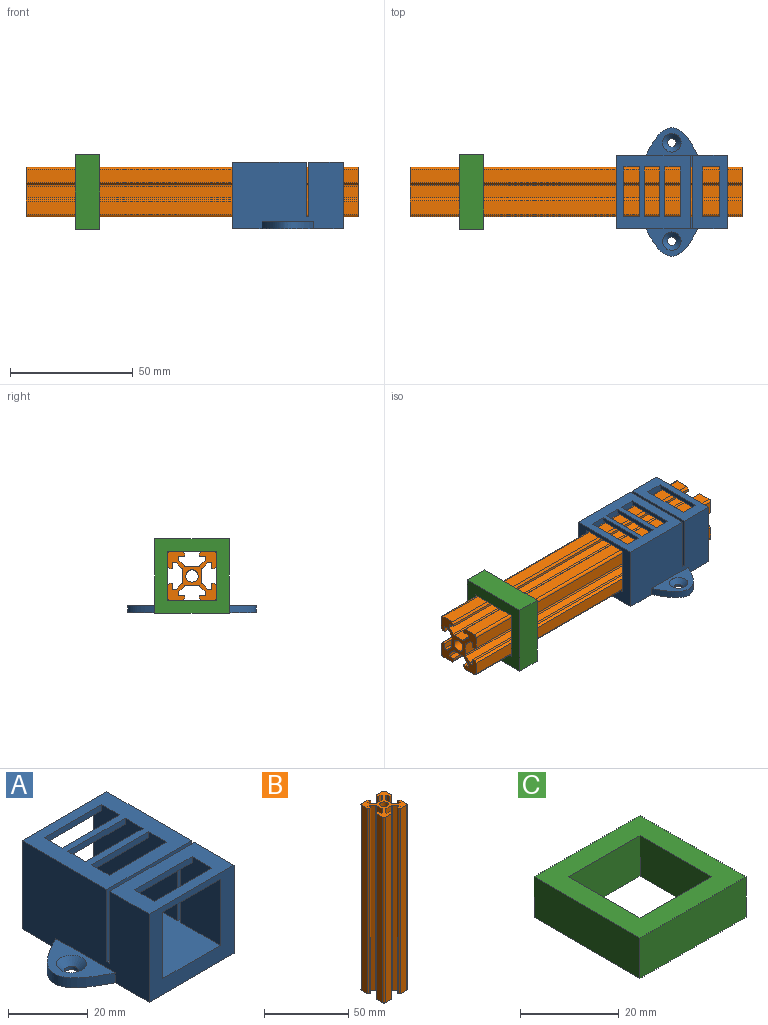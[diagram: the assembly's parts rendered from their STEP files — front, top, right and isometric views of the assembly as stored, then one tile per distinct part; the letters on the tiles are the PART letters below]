
ASSEMBLY  parts=3 mates=2
PART A: 36 faces, bbox 60.4x45x27 mm
  f0: plane 45x27mm, normal (-1,0,0), area 1129.9mm2, adj f2,f3,f11,f12,f13,f14,f16,f22
  f1: plane 45x27mm, normal (1,0,0), area 1129.9mm2, adj f2,f3,f11,f12,f13,f17,f19,f22
  f2: plane 30x30mm, normal (0,0,1), area 514.3mm2, adj f0,f1,f9,f10,f11,f24,f26,f27
  f3: plane 30x14mm, normal (0,0,1), area 277.9mm2, adj f0,f1,f12,f21,f23,f25,f32,f33
  f4: plane 20.3x4mm, normal (0,0,-1), area 81.2mm2, adj f9,f10,f24,f27
  f5: plane 20.3x4mm, normal (0,0,-1), area 81.2mm2, adj f21,f23,f25,f32
  f6: plane 20.3x3mm, normal (0,0,-1), area 60.9mm2, adj f9,f10,f11,f30
  f7: plane 20.3x2mm, normal (0,0,-1), area 40.6mm2, adj f9,f10,f29,f31
  f8: plane 20.3x2mm, normal (0,0,-1), area 40.6mm2, adj f9,f10,f26,f28
  f9: plane 30x22.15mm, normal (1,0,0), area 644.1mm2, adj f2,f4,f6,f7,f8,f11,f22,f24
  f10: plane 30x22.15mm, normal (-1,0,0), area 644.1mm2, adj f2,f4,f6,f7,f8,f11,f22,f24
  f11: plane 30x27mm, normal (0,1,0), area 397.9mm2, adj f0,f1,f2,f6,f9,f10,f13,f22
  f12: plane 30x27mm, normal (0,-1,0), area 397.9mm2, adj f0,f1,f3,f13,f20,f21,f22,f23
  f13: plane 60.43x45mm, normal (0,0,-1), area 1640.4mm2, adj f0,f1,f11,f12,f14,f15,f17,f18
  f14: extruded ~20.98x11.07mm, area 95.7mm2, adj f0,f13,f16
  f15: cylinder r=1.75mm len=3.5mm, axis (0,0,-1), area 11mm2, adj f13,f34
  f16: plane 20.98x15.22mm, normal (0,0,1), area 110.6mm2, adj f0,f14,f34
  f17: extruded ~20.98x11.07mm, area 95.7mm2, adj f1,f13,f19
  f18: cylinder r=1.75mm len=3.5mm, axis (0,0,-1), area 11mm2, adj f13,f35
  f19: plane 20.98x15.22mm, normal (0,0,1), area 110.6mm2, adj f1,f17,f35
  f20: plane 20.3x3mm, normal (0,0,-1), area 60.9mm2, adj f12,f21,f23,f33
  f21: plane 22.15x14mm, normal (1,0,0), area 297.2mm2, adj f3,f5,f12,f20,f22,f25,f32,f33
  f22: plane 45x30mm, normal (0,0,1), area 923.2mm2, adj f0,f1,f9,f10,f11,f12,f21,f23
  f23: plane 22.15x14mm, normal (-1,0,0), area 297.2mm2, adj f3,f5,f12,f20,f22,f25,f32,f33
  f24: plane 30x22.15mm, normal (0,-1,0), area 252.4mm2, adj f0,f1,f2,f4,f9,f10,f22
  f25: plane 30x22.15mm, normal (0,1,0), area 252.4mm2, adj f0,f1,f3,f5,f21,f22,f23
  f26: plane 20.3x1.85mm, normal (0,-1,0), area 37.6mm2, adj f2,f8,f9,f10
  f27: plane 20.3x1.85mm, normal (0,1,0), area 37.6mm2, adj f2,f4,f9,f10
  f28: plane 20.3x1.85mm, normal (0,1,0), area 37.6mm2, adj f2,f8,f9,f10
  f29: plane 20.3x1.85mm, normal (0,-1,0), area 37.6mm2, adj f2,f7,f9,f10
  f30: plane 20.3x1.85mm, normal (0,-1,0), area 37.6mm2, adj f2,f6,f9,f10
  f31: plane 20.3x1.85mm, normal (0,1,0), area 37.6mm2, adj f2,f7,f9,f10
  f32: plane 20.3x1.85mm, normal (0,-1,0), area 37.6mm2, adj f3,f5,f21,f23
  f33: plane 20.3x1.85mm, normal (0,1,0), area 37.6mm2, adj f3,f20,f21,f23
  f34: cone r=1.75mm half-angle=45deg, axis (0,0,1), area 48.9mm2, adj f15,f16
  f35: cone r=3.75mm half-angle=45deg, axis (0,0,1), area 48.9mm2, adj f18,f19
PART B: 75 faces, bbox 20x20x135 mm
  f0: plane 135x1mm, normal (1,0,0), area 135mm2, adj f1,f71,f73,f74
  f1: plane 135x1mm, normal (0.82,0.57,0), area 164.8mm2, adj f0,f2,f73,f74
  f2: plane 135x5.3mm, normal (0,1,0), area 715.5mm2, adj f1,f3,f73,f74
  f3: cylinder r=1mm len=135mm, axis (0,0,-1), area 212.1mm2, adj f2,f4,f73,f74
  f4: plane 135x5.3mm, normal (-1,0,0), area 715.5mm2, adj f3,f5,f73,f74
  f5: plane 135x1mm, normal (-0.57,-0.82,0), area 164.8mm2, adj f4,f6,f73,f74
  f6: plane 135x1mm, normal (0,-1,0), area 135mm2, adj f5,f7,f73,f74
  f7: plane 135x2.5mm, normal (1,0,0), area 337.5mm2, adj f6,f8,f73,f74
  f8: plane 135x1.23mm, normal (0,-1,0), area 166.4mm2, adj f7,f9,f73,f74
  f9: cylinder r=0.5mm len=135mm, axis (0,0,-1), area 53mm2, adj f8,f10,f73,f74
  f10: plane 135x2.22mm, normal (-0.71,-0.71,0), area 424.1mm2, adj f9,f11,f73,f74
  f11: cylinder r=1mm len=135mm, axis (0,0,-1), area 106mm2, adj f10,f12,f73,f74
  f12: plane 135x4.85mm, normal (-1,0,0), area 654.8mm2, adj f11,f13,f73,f74
  f13: cylinder r=1mm len=135mm, axis (0,0,-1), area 106mm2, adj f12,f14,f73,f74
  f14: plane 135x2.22mm, normal (-0.71,0.71,0), area 424.1mm2, adj f13,f15,f73,f74
  f15: cylinder r=0.5mm len=135mm, axis (0,0,-1), area 53mm2, adj f14,f16,f73,f74
  f16: plane 135x1.23mm, normal (0,1,0), area 166.4mm2, adj f15,f17,f73,f74
  f17: plane 135x2.5mm, normal (1,0,0), area 337.5mm2, adj f16,f18,f73,f74
  f18: plane 135x1mm, normal (0,1,0), area 135mm2, adj f17,f19,f73,f74
  f19: plane 135x1mm, normal (-0.57,0.82,0), area 164.8mm2, adj f18,f20,f73,f74
  f20: plane 135x5.3mm, normal (-1,0,0), area 715.5mm2, adj f19,f21,f73,f74
  f21: cylinder r=1mm len=135mm, axis (0,0,-1), area 212.1mm2, adj f20,f22,f73,f74
  f22: plane 135x5.3mm, normal (0,-1,0), area 715.5mm2, adj f21,f23,f73,f74
  f23: plane 135x1mm, normal (0.82,-0.57,0), area 164.8mm2, adj f22,f24,f73,f74
  f24: plane 135x1mm, normal (1,0,0), area 135mm2, adj f23,f25,f73,f74
  f25: plane 135x2.5mm, normal (0,1,0), area 337.5mm2, adj f24,f26,f73,f74
  f26: plane 135x1.23mm, normal (1,0,0), area 166.4mm2, adj f25,f27,f73,f74
  f27: cylinder r=0.5mm len=135mm, axis (0,0,-1), area 53mm2, adj f26,f28,f73,f74
  f28: plane 135x2.22mm, normal (0.71,-0.71,0), area 424.1mm2, adj f27,f29,f73,f74
  f29: cylinder r=1mm len=135mm, axis (0,0,-1), area 106mm2, adj f28,f30,f73,f74
  f30: plane 135x4.85mm, normal (0,-1,0), area 654.8mm2, adj f29,f31,f73,f74
  f31: cylinder r=1mm len=135mm, axis (0,0,-1), area 106mm2, adj f30,f32,f73,f74
  f32: plane 135x2.22mm, normal (-0.71,-0.71,0), area 424.1mm2, adj f31,f33,f73,f74
  f33: cylinder r=0.5mm len=135mm, axis (0,0,-1), area 53mm2, adj f32,f34,f73,f74
  f34: plane 135x1.23mm, normal (-1,0,0), area 166.4mm2, adj f33,f35,f73,f74
  f35: plane 135x2.5mm, normal (0,1,0), area 337.5mm2, adj f34,f36,f73,f74
  f36: plane 135x1mm, normal (-1,0,0), area 135mm2, adj f35,f37,f73,f74
  f37: plane 135x1mm, normal (-0.82,-0.57,0), area 164.8mm2, adj f36,f38,f73,f74
  f38: plane 135x5.3mm, normal (0,-1,0), area 715.5mm2, adj f37,f39,f73,f74
  f39: cylinder r=1mm len=135mm, axis (0,0,-1), area 212.1mm2, adj f38,f40,f73,f74
  f40: plane 135x5.3mm, normal (1,0,0), area 715.5mm2, adj f39,f41,f73,f74
  f41: plane 135x1mm, normal (0.57,0.82,0), area 164.8mm2, adj f40,f42,f73,f74
  f42: plane 135x1mm, normal (0,1,0), area 135mm2, adj f41,f43,f73,f74
  f43: plane 135x2.5mm, normal (-1,0,0), area 337.5mm2, adj f42,f44,f73,f74
  f44: plane 135x1.23mm, normal (0,1,0), area 166.4mm2, adj f43,f45,f73,f74
  f45: cylinder r=0.5mm len=135mm, axis (0,0,-1), area 53mm2, adj f44,f46,f73,f74
  f46: plane 135x2.22mm, normal (0.71,0.71,0), area 424.1mm2, adj f45,f47,f73,f74
  f47: cylinder r=1mm len=135mm, axis (0,0,-1), area 106mm2, adj f46,f48,f73,f74
  f48: plane 135x4.85mm, normal (1,0,0), area 654.8mm2, adj f47,f49,f73,f74
  f49: cylinder r=1mm len=135mm, axis (0,0,-1), area 106mm2, adj f48,f50,f73,f74
  f50: plane 135x2.22mm, normal (0.71,-0.71,0), area 424.1mm2, adj f49,f51,f73,f74
  f51: cylinder r=0.5mm len=135mm, axis (0,0,-1), area 53mm2, adj f50,f52,f73,f74
  f52: plane 135x1.23mm, normal (0,-1,0), area 166.4mm2, adj f51,f53,f73,f74
  f53: plane 135x2.5mm, normal (-1,0,0), area 337.5mm2, adj f52,f54,f73,f74
  f54: plane 135x1mm, normal (0,-1,0), area 135mm2, adj f53,f55,f73,f74
  f55: plane 135x1mm, normal (0.57,-0.82,0), area 164.8mm2, adj f54,f56,f73,f74
  f56: plane 135x5.3mm, normal (1,0,0), area 715.5mm2, adj f55,f57,f73,f74
  f57: cylinder r=1mm len=135mm, axis (0,0,-1), area 212.1mm2, adj f56,f58,f73,f74
  f58: plane 135x5.3mm, normal (0,1,0), area 715.5mm2, adj f57,f59,f73,f74
  f59: plane 135x1mm, normal (-0.82,0.57,0), area 164.8mm2, adj f58,f60,f73,f74
  f60: plane 135x1mm, normal (-1,0,0), area 135mm2, adj f59,f61,f73,f74
  f61: plane 135x2.5mm, normal (0,-1,0), area 337.5mm2, adj f60,f62,f73,f74
  f62: plane 135x1.23mm, normal (-1,0,0), area 166.4mm2, adj f61,f63,f73,f74
  f63: cylinder r=0.5mm len=135mm, axis (0,0,-1), area 53mm2, adj f62,f64,f73,f74
  f64: plane 135x2.22mm, normal (-0.71,0.71,0), area 424.1mm2, adj f63,f65,f73,f74
  f65: cylinder r=1mm len=135mm, axis (0,0,-1), area 106mm2, adj f64,f66,f73,f74
  f66: plane 135x4.85mm, normal (0,1,0), area 654.8mm2, adj f65,f67,f73,f74
  f67: cylinder r=1mm len=135mm, axis (0,0,-1), area 106mm2, adj f66,f68,f73,f74
  f68: plane 135x2.22mm, normal (0.71,0.71,0), area 424.1mm2, adj f67,f69,f73,f74
  f69: cylinder r=0.5mm len=135mm, axis (0,0,-1), area 53mm2, adj f68,f70,f73,f74
  f70: plane 135x1.23mm, normal (1,0,0), area 166.4mm2, adj f69,f71,f73,f74
  f71: plane 135x2.5mm, normal (0,-1,0), area 337.5mm2, adj f0,f70,f73,f74
  f72: cylinder r=2.5mm len=135mm, axis (0,0,-1), area 2120.6mm2, adj f73,f74
  f73: plane 20x20mm, normal (0,0,1), area 176.8mm2, adj f0,f1,f2,f3,f4,f5,f6,f7
  f74: plane 20x20mm, normal (0,0,-1), area 176.8mm2, adj f0,f1,f2,f3,f4,f5,f6,f7
PART C: 10 faces, bbox 30.3x30.3x10 mm
  f0: plane 30.3x10mm, normal (-1,0,0), area 303mm2, adj f1,f7,f8,f9
  f1: plane 30.3x10mm, normal (0,-1,0), area 303mm2, adj f0,f2,f8,f9
  f2: plane 30.3x10mm, normal (1,0,0), area 303mm2, adj f1,f7,f8,f9
  f3: plane 20.3x10mm, normal (-1,0,0), area 203mm2, adj f4,f6,f8,f9
  f4: plane 20.3x10mm, normal (0,1,0), area 203mm2, adj f3,f5,f8,f9
  f5: plane 20.3x10mm, normal (1,0,0), area 203mm2, adj f4,f6,f8,f9
  f6: plane 20.3x10mm, normal (0,-1,0), area 203mm2, adj f3,f5,f8,f9
  f7: plane 30.3x10mm, normal (0,1,0), area 303mm2, adj f0,f2,f8,f9
  f8: plane 30.3x30.3mm, normal (0,0,1), area 506mm2, adj f0,f1,f2,f3,f4,f5,f6,f7
  f9: plane 30.3x30.3mm, normal (0,0,-1), area 506mm2, adj f0,f1,f2,f3,f4,f5,f6,f7
PLACE A rot(axis=(0,0,1),90deg) t=(-38.5,1.57,82.3)mm fixed
PLACE B rot(axis=(0,1,0),90deg) t=(-147.21,-52.91,122.3)mm
PLACE C rot(axis=(-0.58,-0.58,0.58),120deg) t=(-117.21,-52.91,97.3)mm
MATE fastened C.f8 <-> B.f72  axis (-1,0,0) through (-127.21,-52.91,97.3)mm
MATE slider B.f72 <-> A.f12  axis (1,0,0) through (-12.21,-52.91,97.3)mm
